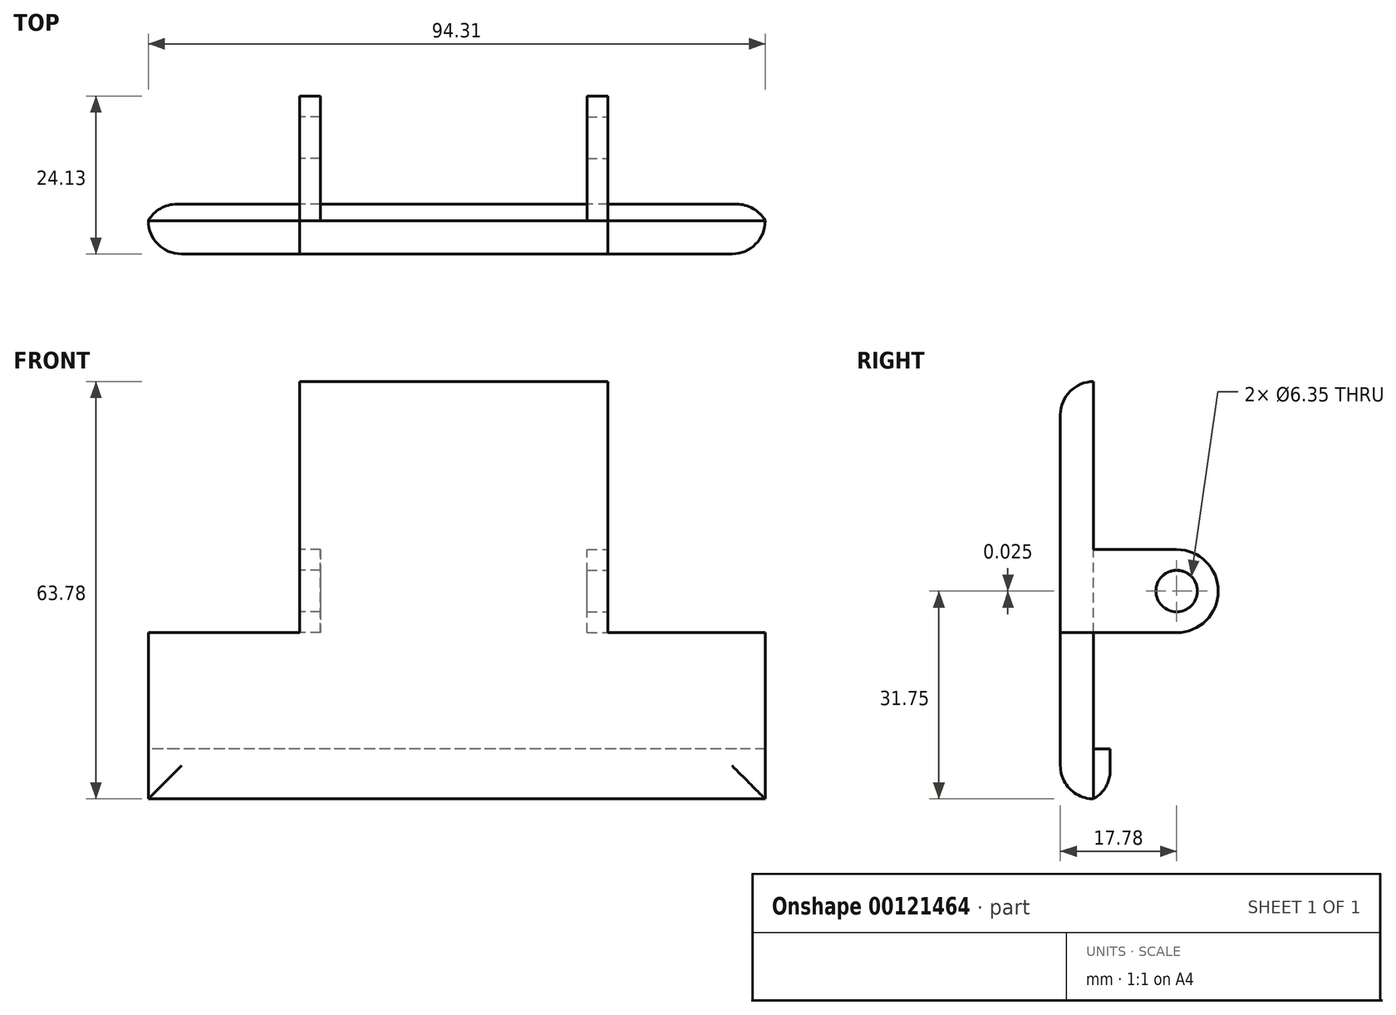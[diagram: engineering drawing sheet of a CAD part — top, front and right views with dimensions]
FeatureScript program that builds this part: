
annotation { "Feature Type Name" : "Feature", "Feature Type Description" : "" }
export const myFeature = defineFeature(function(context is Context, id is Id, definition is map)
    precondition{}
    {
        {
            var Q0;
            Q0=qCreatedBy(makeId("Front.planeOp"),FACE);
            var sketch = newSketch(context, id + "F0", { "sketchPlane" : qUnion([Q0])});
            skLineSegment(sketch, "E0", {"start": v(-23.12, 0) * mm, "end": v(-46.24, 0) * mm});
            skLineSegment(sketch, "E1", {"start": v(-46.24, 0) * mm, "end": v(-46.24, -25.4) * mm});
            skLineSegment(sketch, "E2", {"start": v(-46.24, -25.4) * mm, "end": v(48.07, -25.4) * mm});
            skLineSegment(sketch, "E3", {"start": v(48.07, -25.4) * mm, "end": v(48.07, 0) * mm});
            skLineSegment(sketch, "E4", {"start": v(48.07, 0) * mm, "end": v(24.03, 0) * mm});
            skLineSegment(sketch, "E5", {"start": v(-23.12, 0) * mm, "end": v(-23.12, 38.38) * mm});
            skLineSegment(sketch, "E6", {"start": v(24.03, 0) * mm, "end": v(24.03, 38.38) * mm});
            skLineSegment(sketch, "E7", {"start": v(24.03, 38.38) * mm, "end": v(-23.12, 38.38) * mm});
            skPoint(sketch, "E8.orphan", {"position": v(0, 0) * mm});
            skSolve(sketch);
        }
        {
            var Q0;
            Q0=makeQuery(id+"F0.imprint","IMPRINT",FACE,{"disambiguationData":[TD([[makeQuery(id+"F0.imprint","IMPRINT",EDGE,{"derivedFrom":sQuery(id+"F0.wireOp",EDGE,"E0")}),1.0]])]});
            extrude(context, id + "F1", {"entities" : qUnion([Q0]), "depth" : 5.08 * mm});
        }
        {
            var Q0;
            Q0=makeQuery(id+"F1.opExtrude","CAP_EDGE",EDGE,{"disambiguationData":[OSD([sQuery(id+"F0.wireOp",EDGE,"E1")])],"isStart":false});
            var Q1;
            Q1=makeQuery(id+"F1.opExtrude","CAP_EDGE",EDGE,{"disambiguationData":[OSD([sQuery(id+"F0.wireOp",EDGE,"E3")])],"isStart":false});
            var Q2;
            Q2=makeQuery(id+"F1.opExtrude","CAP_EDGE",EDGE,{"disambiguationData":[OSD([sQuery(id+"F0.wireOp",EDGE,"E2")])],"isStart":false});
            var Q3;
            Q3=makeQuery(id+"F1.opExtrude","CAP_EDGE",EDGE,{"disambiguationData":[OSD([sQuery(id+"F0.wireOp",EDGE,"E7")])],"isStart":false});
            fillet(context, id + "F2", {"entities" : qUnion([Q0, Q1, Q2, Q3]), "radius" : 5.08 * mm, "tangentPropagation" : true, "allowEdgeOverflow" : false});
        }
        {
            var Q0;
            Q0=makeQuery(id+"F1.opExtrude","SWEPT_FACE",FACE,{"disambiguationData":[OSD([sQuery(id+"F0.wireOp",EDGE,"E5")])]});
            var sketch = newSketch(context, id + "F3", { "sketchPlane" : qUnion([Q0])});
            skLineSegment(sketch, "E9", {"start": v(5.08, 0) * mm, "end": v(5.08, 12.7) * mm});
            skLineSegment(sketch, "E10", {"start": v(5.08, 12.7) * mm, "end": v(-12.7, 12.7) * mm});
            skLineSegment(sketch, "E11", {"start": v(-12.7, 0) * mm, "end": v(5.08, 0) * mm});
            skArc(sketch, "E12", {"start": v(-12.7, 12.7) * mm, "mid": v(-19.05, 6.35) * mm, "end": v(-12.7, 0) * mm});
            skCircle(sketch, "E13", {"center": v(-12.7, 6.35) * mm, "radius": 3.18 * mm});
            skSolve(sketch);
        }
        {
            var Q0;
            Q0=makeQuery(id+"F1.opExtrude","SWEPT_FACE",FACE,{"disambiguationData":[OSD([sQuery(id+"F0.wireOp",EDGE,"E6")])]});
            var sketch = newSketch(context, id + "F4", { "sketchPlane" : qUnion([Q0])});
            skLineSegment(sketch, "E14.bottom", {"start": v(-5.08, 0) * mm, "end": v(12.7, 0) * mm});
            skLineSegment(sketch, "E14.top", {"start": v(-5.08, 12.7) * mm, "end": v(12.7, 12.7) * mm});
            skLineSegment(sketch, "E14.left", {"start": v(-5.08, 0) * mm, "end": v(-5.08, 12.7) * mm});
            skCircle(sketch, "E15", {"center": v(12.7, 6.37) * mm, "radius": 3.18 * mm});
            skArc(sketch, "E16", {"start": v(12.7, 0) * mm, "mid": v(19.05, 6.35) * mm, "end": v(12.7, 12.7) * mm});
            skSolve(sketch);
        }
        {
            var Q0;
            Q0=makeQuery(id+"F1.opExtrude","CAP_FACE",FACE,{"disambiguationData":[OSD([sQuery(id+"F0.wireOp",EDGE,"E0"),sQuery(id+"F0.wireOp",EDGE,"E1"),sQuery(id+"F0.wireOp",EDGE,"E2"),sQuery(id+"F0.wireOp",EDGE,"E3"),sQuery(id+"F0.wireOp",EDGE,"E4"),sQuery(id+"F0.wireOp",EDGE,"E5"),sQuery(id+"F0.wireOp",EDGE,"E6"),sQuery(id+"F0.wireOp",EDGE,"E7")])],"isStart":true});
            var sketch = newSketch(context, id + "F5", { "sketchPlane" : qUnion([Q0])});
            skLineSegment(sketch, "E17.bottom", {"start": v(-48.07, -25.4) * mm, "end": v(46.24, -25.4) * mm});
            skLineSegment(sketch, "E17.top", {"start": v(-48.07, -17.78) * mm, "end": v(46.24, -17.78) * mm});
            skLineSegment(sketch, "E17.left", {"start": v(-48.07, -25.4) * mm, "end": v(-48.07, -17.78) * mm});
            skLineSegment(sketch, "E17.right", {"start": v(46.24, -25.4) * mm, "end": v(46.24, -17.78) * mm});
            skSolve(sketch);
        }
        {
            var Q0;
            Q0=makeQuery(id+"F5.imprint","IMPRINT",FACE,{"disambiguationData":[TD([[makeQuery(id+"F5.imprint","IMPRINT",EDGE,{"derivedFrom":sQuery(id+"F5.wireOp",EDGE,"E17.bottom")}),-1.0]])]});
            extrude(context, id + "F6", {"entities" : qUnion([Q0]), "operationType" : NewBodyOperationType.ADD, "depth" : 2.54 * mm});
        }
        {
            var Q0;
            Q0=makeQuery(id+"F6.opExtrude","CAP_EDGE",EDGE,{"disambiguationData":[OSD([sQuery(id+"F5.wireOp",EDGE,"E17.right")])],"isStart":false});
            var Q1;
            Q1=makeQuery(id+"F6.opExtrude","CAP_EDGE",EDGE,{"disambiguationData":[OSD([sQuery(id+"F5.wireOp",EDGE,"E17.bottom")])],"isStart":false});
            var Q2;
            Q2=makeQuery(id+"F6.opExtrude","CAP_EDGE",EDGE,{"disambiguationData":[OSD([sQuery(id+"F5.wireOp",EDGE,"E17.left")])],"isStart":false});
            fillet(context, id + "F7", {"entities" : qUnion([Q0, Q1, Q2]), "radius" : 5.08 * mm, "tangentPropagation" : true, "allowEdgeOverflow" : false});
        }
        {
            var Q0;
            Q0=makeQuery(id+"F4.imprint","IMPRINT",FACE,{"disambiguationData":[TD([[makeQuery(id+"F4.imprint","IMPRINT",EDGE,{"derivedFrom":sQuery(id+"F4.wireOp",EDGE,"E15")}),-1.0]])]});
            extrude(context, id + "F8", {"entities" : qUnion([Q0]), "operationType" : NewBodyOperationType.ADD, "oppositeDirection" : true, "depth" : 3.17 * mm});
        }
        {
            var Q0;
            {var subQ3=sQuery(id+"F3.wireOp",EDGE,"E12");Q0=makeQuery(id+"F3.imprint","IMPRINT",FACE,{"disambiguationData":[TD([[makeQuery(id+"F3.imprint","IMPRINT",EDGE,{"derivedFrom":subQ3}),1.0]])]});}
            extrude(context, id + "F9", {"entities" : qUnion([Q0]), "operationType" : NewBodyOperationType.ADD, "oppositeDirection" : true, "depth" : 3.17 * mm});
        }
    });
